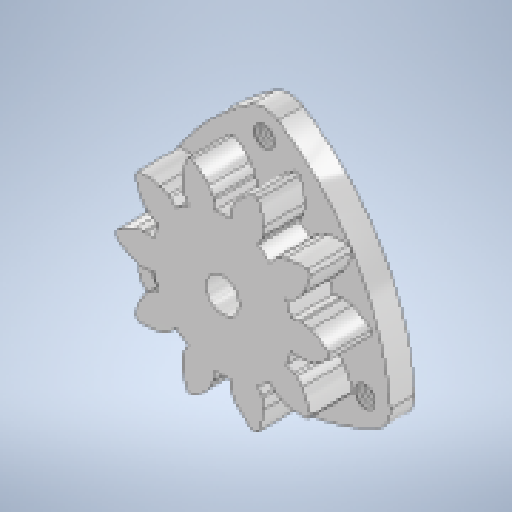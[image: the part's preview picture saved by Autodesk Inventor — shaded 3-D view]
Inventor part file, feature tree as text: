
AUTODESK INVENTOR PART (.ipt)
format: ipt  version: 2023 (Build 270158030, 158C)  size: 347,648 bytes
history: native  units: mm
features: thread x3, extrude x2, sketch x2
ambient origin geometry x8: Origin, YZ Plane, XZ Plane, XY Plane, X Axis, Y Axis, Z Axis, Center Point
bodies: Solid1 (feature_tree)
feature tree (7):
  extrude  "Extrusion1"  Depth=5.0mm
  extrude  "Extrusion2"  Depth=14.0mm
  thread  "Thread1"  [1 undecoded]
  thread  "Thread2"  [1 undecoded]
  thread  "Thread3"  [1 undecoded]
  sketch  "Sketch1"  dims[d0=5.0mm d1=0.0mm d3=2.5mm]
  sketch  "Sketch3"  dims[d4=30.0mm d6=360.0deg d9=40.1mm d11=6.5mm d14=6.0mm d17=6.0mm d18=6.0mm d19=30.0mm d20=30.0mm d22=360.0deg d24=3.0mm d25=0.0mm d26=3.0mm d27=0.0mm d28=3.0mm d29=0.0mm d30=3.0mm d31=0.0mm d32=4.0mm d33=4.0mm d34=14.0mm]
note: 3 required parameter values undecoded (feature->parameter linkage not recoverable at this tier; creation-order binding heuristic only, values carry confidence <= 0.55)
